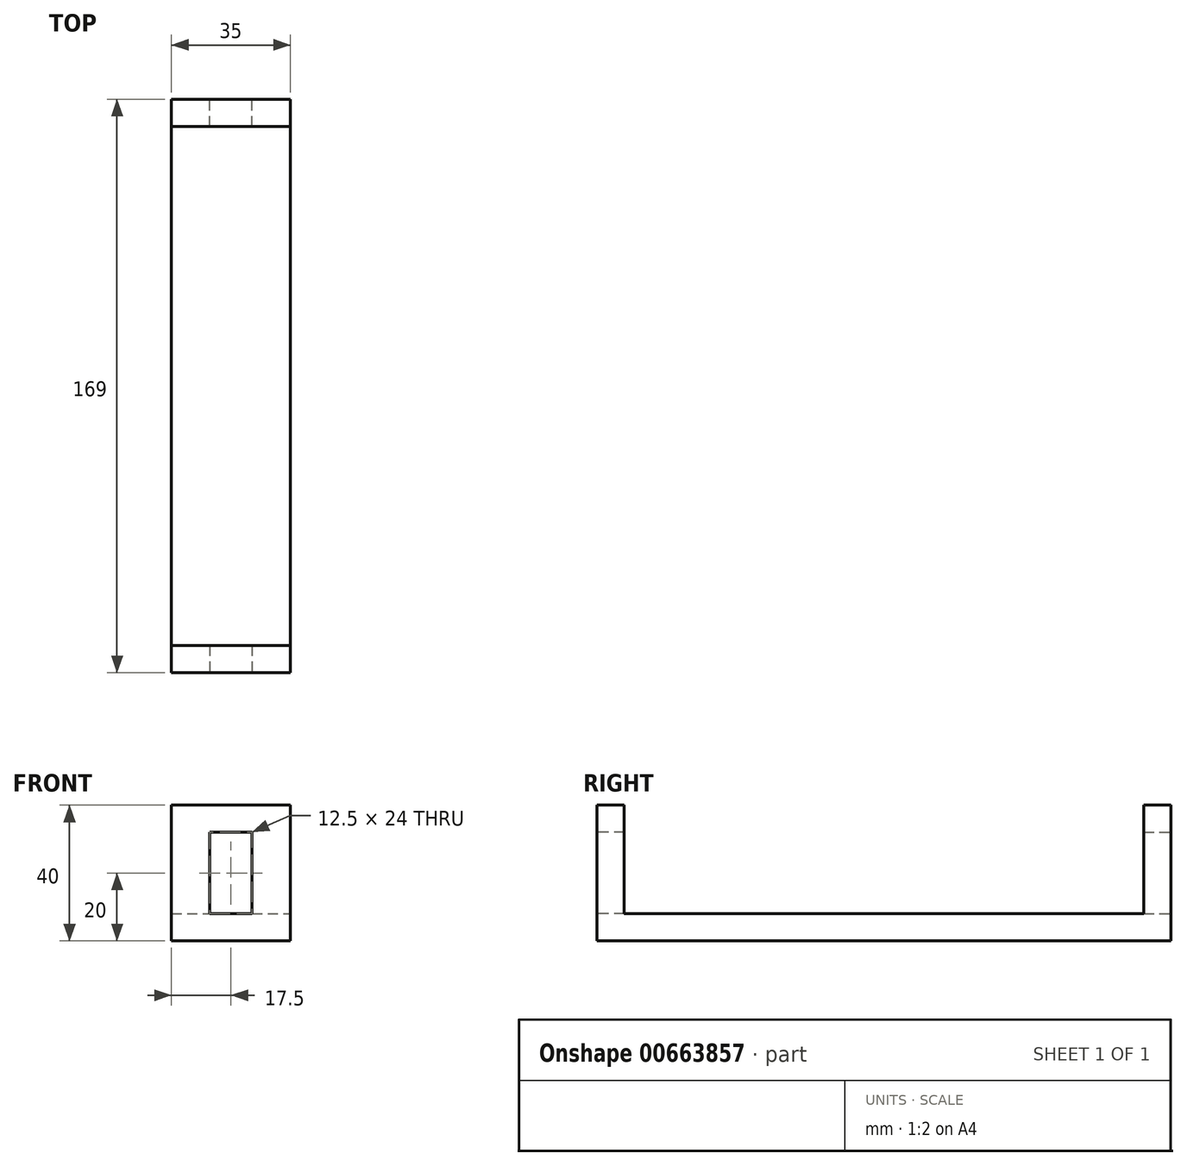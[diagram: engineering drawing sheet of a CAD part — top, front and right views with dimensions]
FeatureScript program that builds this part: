
annotation { "Feature Type Name" : "Feature", "Feature Type Description" : "" }
export const myFeature = defineFeature(function(context is Context, id is Id, definition is map)
    precondition{}
    {
        {
            var Q0;
            Q0=qCreatedBy(makeId("Top.planeOp"),FACE);
            var sketch = newSketch(context, id + "F0", { "sketchPlane" : qUnion([Q0])});
            skLineSegment(sketch, "E0.bottom", {"start": v(-17.5, 0) * mm, "end": v(17.5, 0) * mm});
            skLineSegment(sketch, "E0.top", {"start": v(-17.5, -76.5) * mm, "end": v(17.5, -76.5) * mm});
            skLineSegment(sketch, "E0.left", {"start": v(-17.5, 0) * mm, "end": v(-17.5, -76.5) * mm});
            skLineSegment(sketch, "E0.right", {"start": v(17.5, 0) * mm, "end": v(17.5, -76.5) * mm});
            skSolve(sketch);
        }
        {
            var Q0;
            Q0=makeQuery(id+"F0.imprint","IMPRINT",FACE,{"disambiguationData":[TD([[makeQuery(id+"F0.imprint","IMPRINT",EDGE,{"derivedFrom":sQuery(id+"F0.wireOp",EDGE,"E0.bottom")}),-1.0]])]});
            extrude(context, id + "F1", {"entities" : qUnion([Q0]), "depth" : 8 * mm, "offsetDistance" : 25 * mm});
        }
        {
            var Q0;
            Q0=makeQuery(id+"F1.opExtrude","SWEPT_FACE",FACE,{"disambiguationData":[OSD([sQuery(id+"F0.wireOp",EDGE,"E0.top")])]});
            var sketch = newSketch(context, id + "F2", { "sketchPlane" : qUnion([Q0])});
            skLineSegment(sketch, "E1.bottom", {"start": v(-17.5, 40) * mm, "end": v(17.5, 40) * mm});
            skLineSegment(sketch, "E1.top", {"start": v(-17.5, 0) * mm, "end": v(17.5, 0) * mm});
            skLineSegment(sketch, "E1.left", {"start": v(-17.5, 40) * mm, "end": v(-17.5, 0) * mm});
            skLineSegment(sketch, "E1.right", {"start": v(17.5, 40) * mm, "end": v(17.5, 0) * mm});
            skSolve(sketch);
        }
        {
            var Q0;
            Q0=makeQuery(id+"F1.opExtrude","SWEPT_FACE",FACE,{"disambiguationData":[OSD([sQuery(id+"F0.wireOp",EDGE,"E0.top")])]});
            var Q1;
            Q1=makeQuery(id+"F1.opExtrude","SWEPT_FACE",FACE,{"disambiguationData":[OSD([sQuery(id+"F0.wireOp",EDGE,"E0.bottom")])]});
            var Q2;
            Q2 = qSketchRegion(id + "F2", true);
            extrude(context, id + "F3", {"entities" : qUnion([Q0, Q1, Q2]), "operationType" : NewBodyOperationType.ADD, "depth" : 8 * mm, "offsetDistance" : 25 * mm});
        }
        {
            var Q0;
            Q0=makeQuery(id+"F3.boolean.opBoolean","MERGE",FACE,{"derivedFrom":[makeQuery(id+"F3.opExtrude","CAP_FACE",FACE,{"disambiguationData":[OSD([sQuery(id+"F0.wireOp",EDGE,"E0.top")])],"isStart":false}),makeQuery(id+"F3.opExtrude","CAP_FACE",FACE,{"disambiguationData":[OSD([sQuery(id+"F2.wireOp",EDGE,"E1.bottom"),sQuery(id+"F2.wireOp",EDGE,"E1.top"),sQuery(id+"F2.wireOp",EDGE,"E1.left"),sQuery(id+"F2.wireOp",EDGE,"E1.right")])],"isStart":false})]});
            var sketch = newSketch(context, id + "F4", { "sketchPlane" : qUnion([Q0])});
            skLineSegment(sketch, "E2", {"start": v(17.5, 0) * mm, "end": v(-17.5, 40) * mm, "construction": true});
            skLineSegment(sketch, "E3", {"start": v(-17.5, 0) * mm, "end": v(17.5, 40) * mm, "construction": true});
            skPoint(sketch, "E4", {"position": v(0, 20) * mm});
            skPoint(sketch, "E5", {"position": v(-2.87, 23.28) * mm});
            skLineSegment(sketch, "E6.bottom", {"start": v(6.25, 8) * mm, "end": v(-6.25, 8) * mm});
            skLineSegment(sketch, "E6.top", {"start": v(6.25, 32) * mm, "end": v(-6.25, 32) * mm});
            skLineSegment(sketch, "E6.left", {"start": v(6.25, 8) * mm, "end": v(6.25, 32) * mm});
            skLineSegment(sketch, "E6.right", {"start": v(-6.25, 8) * mm, "end": v(-6.25, 32) * mm});
            skSolve(sketch);
        }
        {
            var Q0;
            Q0=makeQuery(id+"F4.imprint","IMPRINT",FACE,{"disambiguationData":[TD([[makeQuery(id+"F4.imprint","IMPRINT",EDGE,{"derivedFrom":sQuery(id+"F4.wireOp",EDGE,"E6.bottom")}),-1.0]])]});
            extrude(context, id + "F5", {"entities" : qUnion([Q0]), "operationType" : NewBodyOperationType.REMOVE, "endBound" : BoundingType.THROUGH_ALL, "oppositeDirection" : true, "depth" : 25 * mm, "offsetDistance" : 25 * mm});
        }
        {
            var Q0;
            Q0=makeQuery(id+"F1.opExtrude","SWEPT_BODY",BODY,{"disambiguationData":[OSD([sQuery(id+"F0.wireOp",EDGE,"E0.bottom"),sQuery(id+"F0.wireOp",EDGE,"E0.top"),sQuery(id+"F0.wireOp",EDGE,"E0.left"),sQuery(id+"F0.wireOp",EDGE,"E0.right")])]});
            var Q1;
            Q1=makeQuery(id+"F1.opExtrude","SWEPT_FACE",FACE,{"disambiguationData":[OSD([sQuery(id+"F0.wireOp",EDGE,"E0.bottom")])]});
            mirror(context, id + "F6", {"operationType" : NewBodyOperationType.ADD, "entities" : qUnion([Q0]), "mirrorPlane" : qUnion([Q1])});
        }
    });
